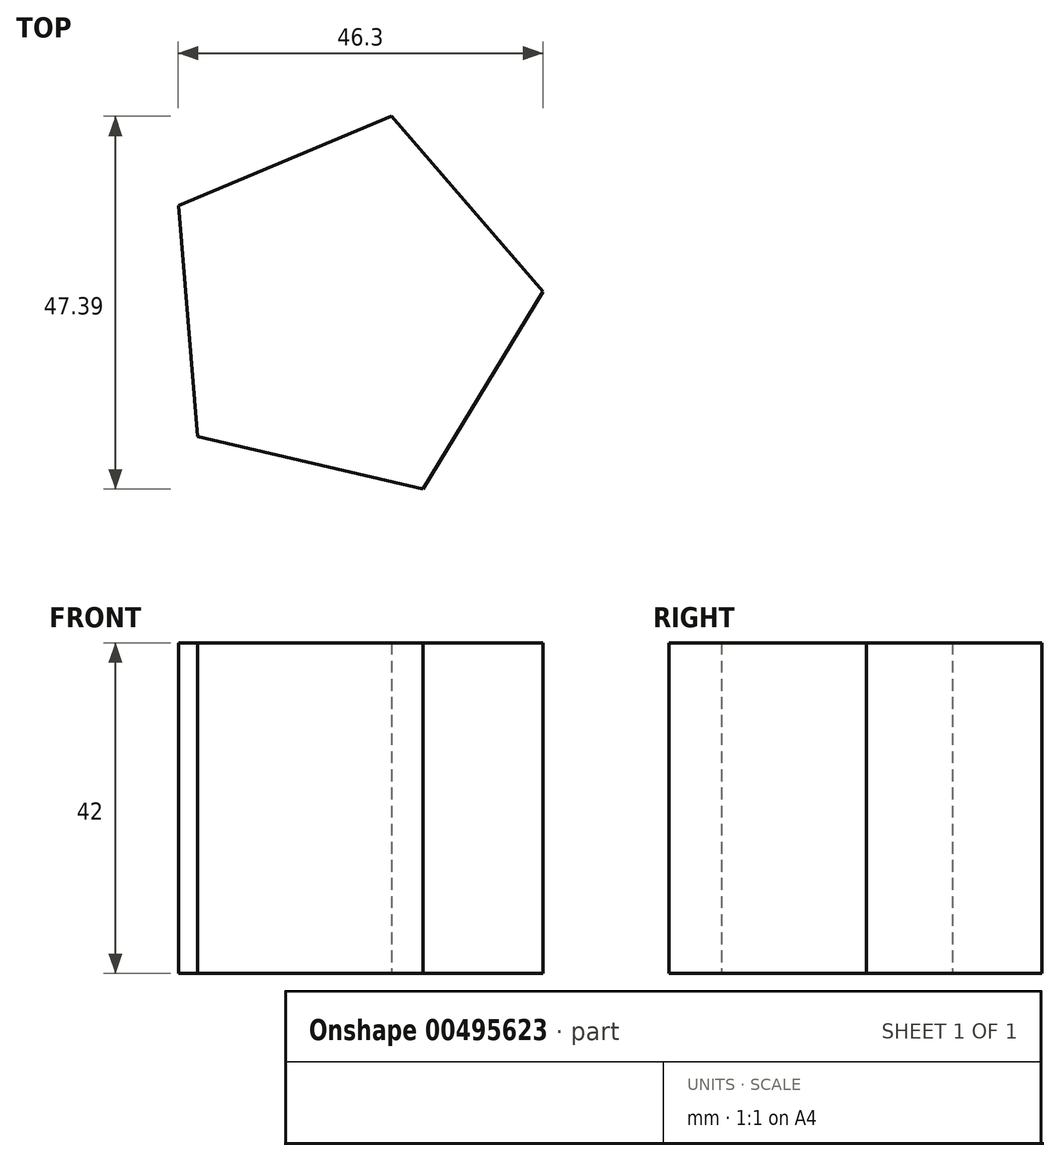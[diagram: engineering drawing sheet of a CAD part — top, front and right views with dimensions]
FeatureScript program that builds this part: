
annotation { "Feature Type Name" : "Feature", "Feature Type Description" : "" }
export const myFeature = defineFeature(function(context is Context, id is Id, definition is map)
    precondition{}
    {
        {
            var Q0;
            Q0=qCreatedBy(makeId("Top.planeOp"),FACE);
            var sketch = newSketch(context, id + "F0", { "sketchPlane" : qUnion([Q0])});
            skCircle(sketch, "E0.cCircle", {"center": v(-16.71, 24.29) * mm, "radius": 20.23 * mm, "construction": true});
            skLineSegment(sketch, "E0.0", {"start": v(8.2, 26.37) * mm, "end": v(-7.03, 1.24) * mm});
            skLineSegment(sketch, "E0.1", {"start": v(-7.03, 1.24) * mm, "end": v(-35.64, 7.95) * mm});
            skLineSegment(sketch, "E0.2", {"start": v(-35.64, 7.95) * mm, "end": v(-38.1, 37.24) * mm});
            skLineSegment(sketch, "E0.3", {"start": v(-38.1, 37.24) * mm, "end": v(-11, 48.63) * mm});
            skLineSegment(sketch, "E0.4", {"start": v(-11, 48.63) * mm, "end": v(8.2, 26.37) * mm});
            skPoint(sketch, "E0.0.midPoint", {"position": v(0.59, 13.8) * mm});
            skSolve(sketch);
        }
        {
            var Q0;
            Q0=makeQuery(id+"F0.imprint","IMPRINT",FACE,{"disambiguationData":[TD([[makeQuery(id+"F0.imprint","IMPRINT",EDGE,{"derivedFrom":sQuery(id+"F0.wireOp",EDGE,"E0.0")}),-1.0]])]});
            extrude(context, id + "F1", {"entities" : qUnion([Q0]), "depth" : 42 * mm});
        }
    });
